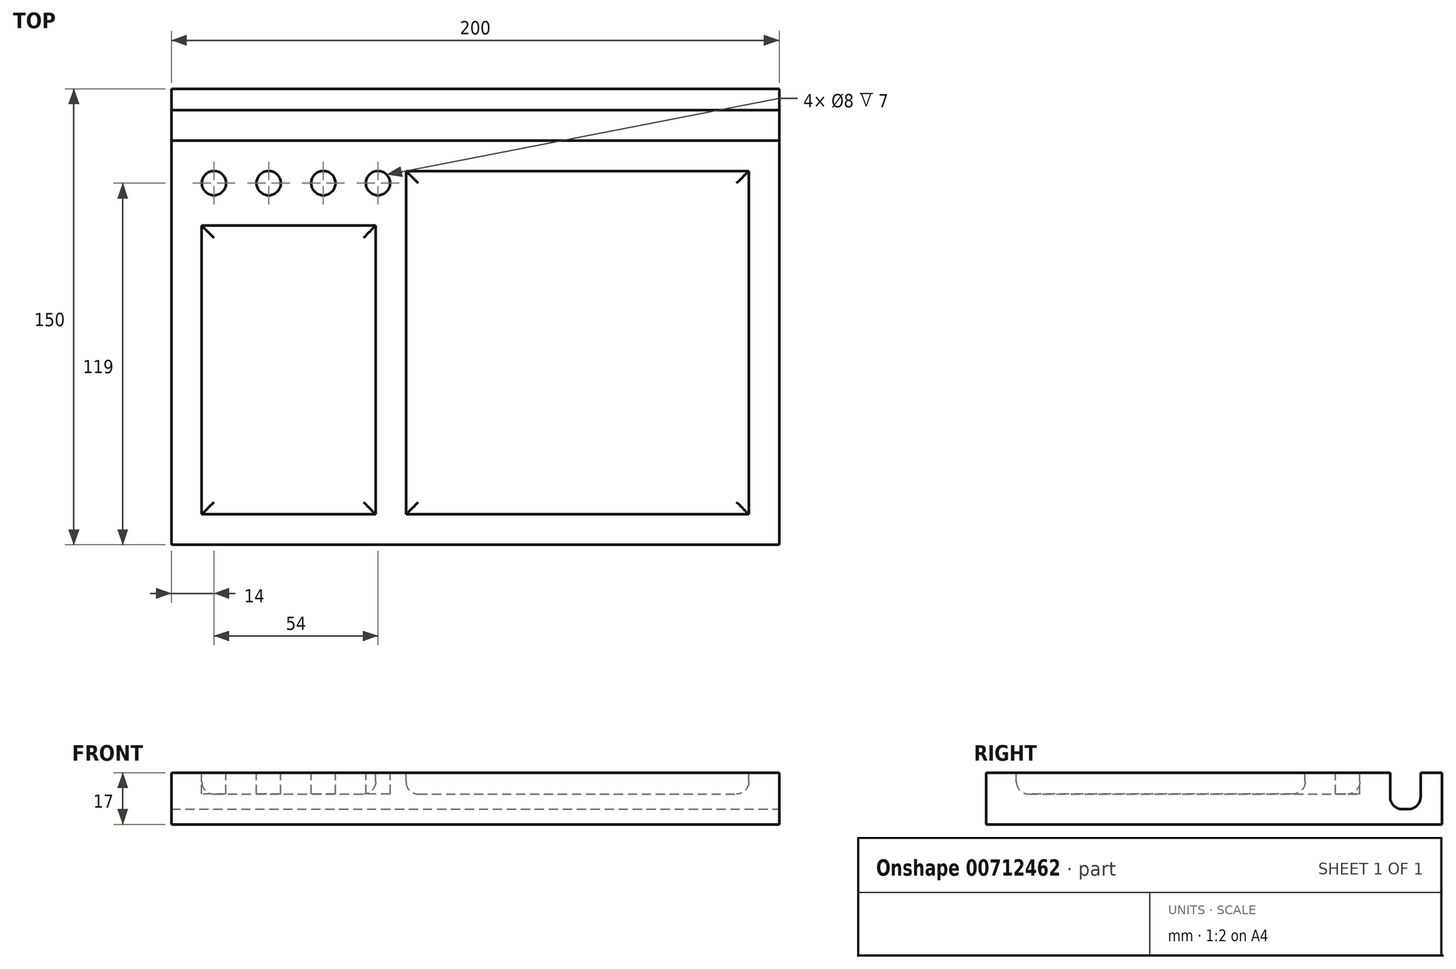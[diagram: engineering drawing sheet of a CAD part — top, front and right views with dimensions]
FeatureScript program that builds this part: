
annotation { "Feature Type Name" : "Feature", "Feature Type Description" : "" }
export const myFeature = defineFeature(function(context is Context, id is Id, definition is map)
    precondition{}
    {
        {
            var Q0;
            Q0=qCreatedBy(makeId("Top.planeOp"),FACE);
            var sketch = newSketch(context, id + "F0", { "sketchPlane" : qUnion([Q0])});
            skLineSegment(sketch, "E0.bottom", {"start": v(200, 150) * mm, "end": v(0, 150) * mm});
            skLineSegment(sketch, "E0.top", {"start": v(200, 0) * mm, "end": v(0, 0) * mm});
            skLineSegment(sketch, "E0.left", {"start": v(200, 150) * mm, "end": v(200, 0) * mm});
            skLineSegment(sketch, "E0.right", {"start": v(0, 150) * mm, "end": v(0, 0) * mm});
            skSolve(sketch);
        }
        {
            var Q0;
            Q0=makeQuery(id+"F0.imprint","IMPRINT",FACE,{"disambiguationData":[TD([[makeQuery(id+"F0.imprint","IMPRINT",EDGE,{"derivedFrom":sQuery(id+"F0.wireOp",EDGE,"E0.bottom")}),1.0]])]});
            extrude(context, id + "F1", {"entities" : qUnion([Q0]), "depth" : 17 * mm, "offsetDistance" : 25 * mm});
        }
        {
            var Q0;
            Q0=makeQuery(id+"F1.opExtrude","CAP_FACE",FACE,{"disambiguationData":[OSD([sQuery(id+"F0.wireOp",EDGE,"E0.bottom"),sQuery(id+"F0.wireOp",EDGE,"E0.top"),sQuery(id+"F0.wireOp",EDGE,"E0.left"),sQuery(id+"F0.wireOp",EDGE,"E0.right")])],"isStart":false});
            var sketch = newSketch(context, id + "F2", { "sketchPlane" : qUnion([Q0])});
            skCircle(sketch, "E1", {"center": v(14, 119) * mm, "radius": 4 * mm});
            skLineSegment(sketch, "E2", {"start": v(0, 143) * mm, "end": v(200, 143) * mm});
            skLineSegment(sketch, "E3", {"start": v(0, 133) * mm, "end": v(200, 133) * mm});
            skLineSegment(sketch, "E4.bottom", {"start": v(77.22, 10) * mm, "end": v(190, 10) * mm});
            skLineSegment(sketch, "E4.top", {"start": v(77.22, 123) * mm, "end": v(190, 123) * mm});
            skLineSegment(sketch, "E4.left", {"start": v(77.22, 10) * mm, "end": v(77.22, 123) * mm});
            skLineSegment(sketch, "E4.right", {"start": v(190, 10) * mm, "end": v(190, 123) * mm});
            skLineSegment(sketch, "E5.bottom", {"start": v(10, 105) * mm, "end": v(67.22, 105) * mm});
            skLineSegment(sketch, "E5.top", {"start": v(10, 10) * mm, "end": v(67.22, 10) * mm});
            skLineSegment(sketch, "E5.left", {"start": v(10, 105) * mm, "end": v(10, 10) * mm});
            skLineSegment(sketch, "E5.right", {"start": v(67.22, 105) * mm, "end": v(67.22, 10) * mm});
            skLineSegment(sketch, "E6", {"start": v(0, 75) * mm, "end": v(200, 75) * mm, "construction": true});
            skCircle(sketch, "E7", {"center": v(32, 119) * mm, "radius": 4 * mm});
            skCircle(sketch, "E8", {"center": v(50, 119) * mm, "radius": 4 * mm});
            skCircle(sketch, "E9", {"center": v(68, 119) * mm, "radius": 4 * mm});
            skSolve(sketch);
        }
        {
            var Q0;
            {var subQ0=sQuery(id+"F2.wireOp",EDGE,"E2");Q0=makeQuery(id+"F2.imprint","IMPRINT",FACE,{"disambiguationData":[TD([[makeQuery(id+"F2.imprint","IMPRINT",EDGE,{"derivedFrom":subQ0}),-1.0]])]});}
            extrude(context, id + "F3", {"entities" : qUnion([Q0]), "operationType" : NewBodyOperationType.REMOVE, "oppositeDirection" : true, "depth" : 12 * mm, "offsetDistance" : 25 * mm});
        }
        {
            var Q0;
            Q0=makeQuery(id+"F2.imprint","IMPRINT",FACE,{"disambiguationData":[TD([[makeQuery(id+"F2.imprint","IMPRINT",EDGE,{"derivedFrom":sQuery(id+"F2.wireOp",EDGE,"E1")}),1.0]])]});
            var Q1;
            Q1=makeQuery(id+"F2.imprint","IMPRINT",FACE,{"disambiguationData":[TD([[makeQuery(id+"F2.imprint","IMPRINT",EDGE,{"derivedFrom":sQuery(id+"F2.wireOp",EDGE,"E7")}),1.0]])]});
            var Q2;
            Q2=makeQuery(id+"F2.imprint","IMPRINT",FACE,{"disambiguationData":[TD([[makeQuery(id+"F2.imprint","IMPRINT",EDGE,{"derivedFrom":sQuery(id+"F2.wireOp",EDGE,"E8")}),1.0]])]});
            var Q3;
            Q3=makeQuery(id+"F2.imprint","IMPRINT",FACE,{"disambiguationData":[TD([[makeQuery(id+"F2.imprint","IMPRINT",EDGE,{"derivedFrom":sQuery(id+"F2.wireOp",EDGE,"E9")}),1.0]])]});
            var Q4;
            Q4=makeQuery(id+"F2.imprint","IMPRINT",FACE,{"disambiguationData":[TD([[makeQuery(id+"F2.imprint","IMPRINT",EDGE,{"derivedFrom":sQuery(id+"F2.wireOp",EDGE,"E5.bottom")}),-1.0]])]});
            var Q5;
            Q5=makeQuery(id+"F2.imprint","IMPRINT",FACE,{"disambiguationData":[TD([[makeQuery(id+"F2.imprint","IMPRINT",EDGE,{"derivedFrom":sQuery(id+"F2.wireOp",EDGE,"E4.bottom")}),1.0]])]});
            extrude(context, id + "F4", {"entities" : qUnion([Q0, Q1, Q2, Q3, Q4, Q5]), "operationType" : NewBodyOperationType.REMOVE, "oppositeDirection" : true, "depth" : 7 * mm, "offsetDistance" : 25 * mm});
        }
        {
            var Q0;
            Q0=makeQuery(id+"F4.boolean.opBoolean","COPY",EDGE,{"derivedFrom":makeQuery(id+"F4.opExtrude","CAP_EDGE",EDGE,{"disambiguationData":[OSD([sQuery(id+"F2.wireOp",EDGE,"E4.top")])],"isStart":false})});
            var Q1;
            Q1=makeQuery(id+"F4.boolean.opBoolean","COPY",EDGE,{"derivedFrom":makeQuery(id+"F4.opExtrude","CAP_EDGE",EDGE,{"disambiguationData":[OSD([sQuery(id+"F2.wireOp",EDGE,"E4.left")])],"isStart":false})});
            var Q2;
            Q2=makeQuery(id+"F4.boolean.opBoolean","COPY",EDGE,{"derivedFrom":makeQuery(id+"F4.opExtrude","CAP_EDGE",EDGE,{"disambiguationData":[OSD([sQuery(id+"F2.wireOp",EDGE,"E4.bottom")])],"isStart":false})});
            var Q3;
            Q3=makeQuery(id+"F4.boolean.opBoolean","COPY",EDGE,{"derivedFrom":makeQuery(id+"F4.opExtrude","CAP_EDGE",EDGE,{"disambiguationData":[OSD([sQuery(id+"F2.wireOp",EDGE,"E4.right")])],"isStart":false})});
            fillet(context, id + "F5", {"entities" : qUnion([Q0, Q1, Q2, Q3]), "radius" : 4 * mm, "tangentPropagation" : true, "allowEdgeOverflow" : false});
        }
        {
            var Q0;
            Q0=makeQuery(id+"F3.boolean.opBoolean","COPY",EDGE,{"derivedFrom":makeQuery(id+"F3.opExtrude","CAP_EDGE",EDGE,{"disambiguationData":[OSD([sQuery(id+"F2.wireOp",EDGE,"E2")])],"isStart":false})});
            var Q1;
            Q1=makeQuery(id+"F3.boolean.opBoolean","COPY",EDGE,{"derivedFrom":makeQuery(id+"F3.opExtrude","CAP_EDGE",EDGE,{"disambiguationData":[OSD([sQuery(id+"F2.wireOp",EDGE,"E3")])],"isStart":false})});
            fillet(context, id + "F6", {"entities" : qUnion([Q0, Q1]), "radius" : 4 * mm, "tangentPropagation" : true, "allowEdgeOverflow" : false});
        }
        {
            var Q0;
            Q0=makeQuery(id+"F4.boolean.opBoolean","COPY",EDGE,{"derivedFrom":makeQuery(id+"F4.opExtrude","CAP_EDGE",EDGE,{"disambiguationData":[OSD([sQuery(id+"F2.wireOp",EDGE,"E5.left")])],"isStart":false})});
            var Q1;
            Q1=makeQuery(id+"F4.boolean.opBoolean","COPY",EDGE,{"derivedFrom":makeQuery(id+"F4.opExtrude","CAP_EDGE",EDGE,{"disambiguationData":[OSD([sQuery(id+"F2.wireOp",EDGE,"E5.bottom")])],"isStart":false})});
            var Q2;
            Q2=makeQuery(id+"F4.boolean.opBoolean","COPY",EDGE,{"derivedFrom":makeQuery(id+"F4.opExtrude","CAP_EDGE",EDGE,{"disambiguationData":[OSD([sQuery(id+"F2.wireOp",EDGE,"E5.right")])],"isStart":false})});
            var Q3;
            Q3=makeQuery(id+"F4.boolean.opBoolean","COPY",EDGE,{"derivedFrom":makeQuery(id+"F4.opExtrude","CAP_EDGE",EDGE,{"disambiguationData":[OSD([sQuery(id+"F2.wireOp",EDGE,"E5.top")])],"isStart":false})});
            fillet(context, id + "F7", {"entities" : qUnion([Q0, Q1, Q2, Q3]), "radius" : 4 * mm, "tangentPropagation" : true, "allowEdgeOverflow" : false});
        }
    });
